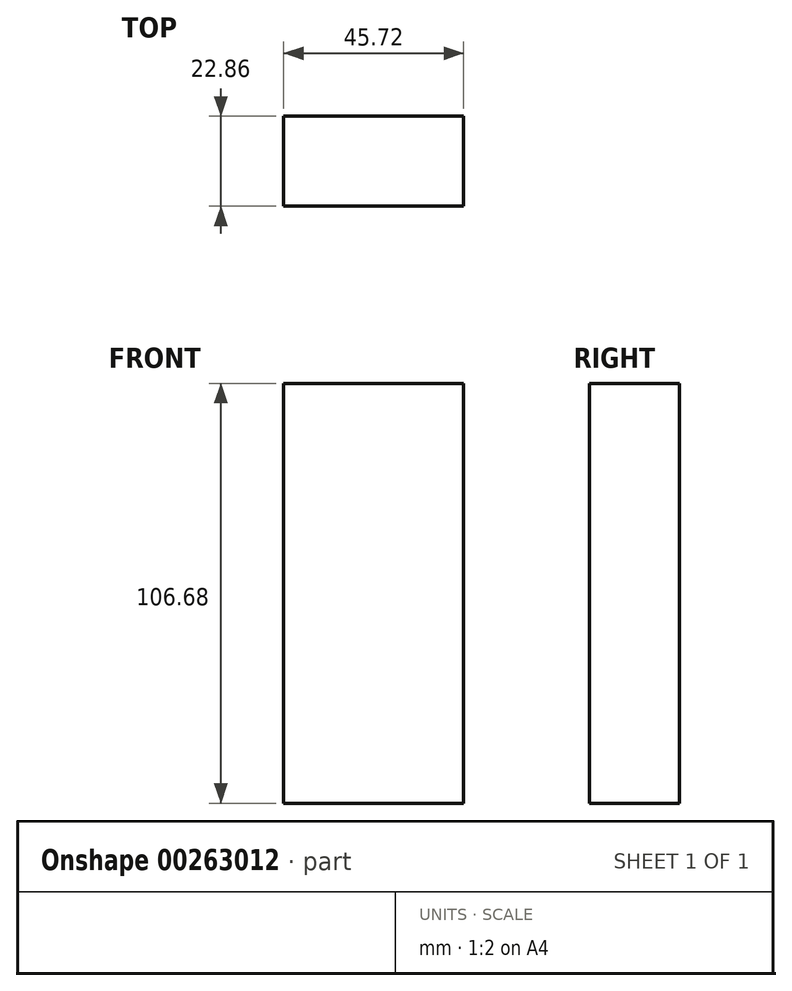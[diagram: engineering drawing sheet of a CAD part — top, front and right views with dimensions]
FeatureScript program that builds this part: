
annotation { "Feature Type Name" : "Feature", "Feature Type Description" : "" }
export const myFeature = defineFeature(function(context is Context, id is Id, definition is map)
    precondition{}
    {
        {
            var Q0;
            Q0=qCreatedBy(makeId("Front.planeOp"),FACE);
            var sketch = newSketch(context, id + "F0", { "sketchPlane" : qUnion([Q0])});
            skLineSegment(sketch, "E0.bottom", {"start": v(4.7, 61.9) * mm, "end": v(-41.02, 61.9) * mm});
            skLineSegment(sketch, "E0.top", {"start": v(4.7, -44.78) * mm, "end": v(-41.02, -44.78) * mm});
            skLineSegment(sketch, "E0.left", {"start": v(4.7, 61.9) * mm, "end": v(4.7, -44.78) * mm});
            skLineSegment(sketch, "E0.right", {"start": v(-41.02, 61.9) * mm, "end": v(-41.02, -44.78) * mm});
            skSolve(sketch);
        }
        {
            var Q0;
            Q0 = qSketchRegion(id + "F0", true);
            extrude(context, id + "F1", {"entities" : qUnion([Q0]), "depth" : 22.86 * mm});
        }
    });
